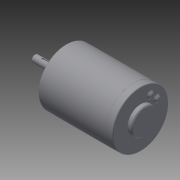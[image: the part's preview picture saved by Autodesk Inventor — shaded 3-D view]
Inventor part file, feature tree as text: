
AUTODESK INVENTOR PART (.ipt)
format: ipt  version: 2014 (Build 180170000, 170)  size: 162,816 bytes
history: native  units: in
note: dims shown in document units (in); Inventor stores cm internally (conversion verified against a paired STEP export)
features: chamfer x1, other x1, imported_body x1
ambient origin geometry x8: Origin, YZ Plane, XZ Plane, XY Plane, X Axis, Y Axis, Z Axis, Center Point
bodies: Body1 (feature_tree)
feature tree (3):
  chamfer  "Chamfer3"  [1 undecoded]
  other  "217-3371-STEP1"
  imported_body  "Base1"
note: 1 required parameter value undecoded (feature->parameter linkage not recoverable at this tier; creation-order binding heuristic only, values carry confidence <= 0.55)
